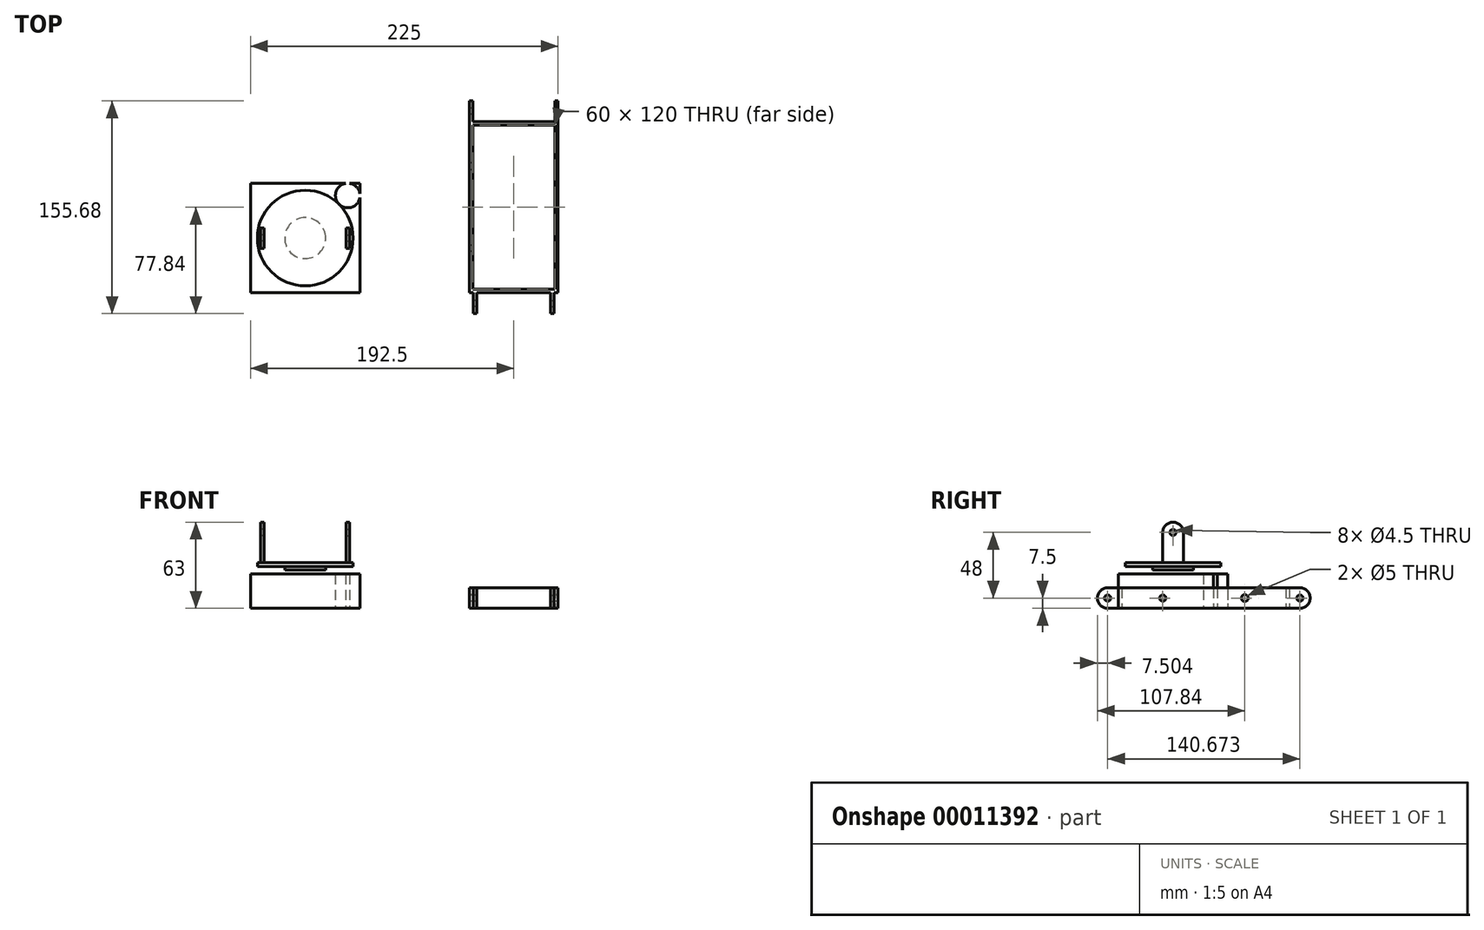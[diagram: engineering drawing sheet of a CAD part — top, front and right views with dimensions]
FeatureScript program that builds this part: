
annotation { "Feature Type Name" : "Feature", "Feature Type Description" : "" }
export const myFeature = defineFeature(function(context is Context, id is Id, definition is map)
    precondition{}
    {
        {
            var Q0;
            Q0=qCreatedBy(makeId("Top.planeOp"),FACE);
            var sketch = newSketch(context, id + "F0", { "sketchPlane" : qUnion([Q0])});
            skLineSegment(sketch, "E0.bottom", {"start": v(0, 120) * mm, "end": v(60, 120) * mm});
            skLineSegment(sketch, "E0.top", {"start": v(0, 0) * mm, "end": v(60, 0) * mm});
            skLineSegment(sketch, "E0.left", {"start": v(0, 120) * mm, "end": v(0, 0) * mm});
            skLineSegment(sketch, "E0.right", {"start": v(60, 120) * mm, "end": v(60, 0) * mm});
            skLineSegment(sketch, "E1", {"start": v(0, 90) * mm, "end": v(60, 90) * mm, "construction": true});
            skLineSegment(sketch, "E2", {"start": v(0, 30) * mm, "end": v(60, 30) * mm, "construction": true});
            skLineSegment(sketch, "E3.0", {"start": v(-2.5, 122.5) * mm, "end": v(62.5, 122.5) * mm});
            skLineSegment(sketch, "E3.1", {"start": v(-2.5, 122.5) * mm, "end": v(-2.5, -2.5) * mm});
            skLineSegment(sketch, "E3.2", {"start": v(-2.5, -2.5) * mm, "end": v(62.5, -2.5) * mm});
            skLineSegment(sketch, "E3.3", {"start": v(62.5, 122.5) * mm, "end": v(62.5, -2.5) * mm});
            skSolve(sketch);
        }
        {
            var Q0;
            Q0=makeQuery(id+"F0.imprint","IMPRINT",FACE,{"disambiguationData":[TD([[makeQuery(id+"F0.imprint","IMPRINT",EDGE,{"derivedFrom":sQuery(id+"F0.wireOp",EDGE,"E0.bottom")}),1.0]])]});
            extrude(context, id + "F1", {"entities" : qUnion([Q0]), "depth" : 15 * mm});
        }
        {
            var Q0;
            Q0=makeQuery(id+"F1.opExtrude","SWEPT_FACE",FACE,{"disambiguationData":[OSD([sQuery(id+"F0.wireOp",EDGE,"E3.1")])]});
            var sketch = newSketch(context, id + "F2", { "sketchPlane" : qUnion([Q0])});
            skLineSegment(sketch, "E4", {"start": v(-30, 0) * mm, "end": v(-30, 15) * mm, "construction": true});
            skCircle(sketch, "E5", {"center": v(-30, 7.5) * mm, "radius": 2.25 * mm});
            skLineSegment(sketch, "E6", {"start": v(-90, 0) * mm, "end": v(-90, 15) * mm, "construction": true});
            skCircle(sketch, "E7", {"center": v(-90, 7.5) * mm, "radius": 2.25 * mm});
            skLineSegment(sketch, "E8.bottom", {"start": v(-122.5, 0) * mm, "end": v(-130.34, 0) * mm});
            skLineSegment(sketch, "E8.top", {"start": v(-122.5, 15) * mm, "end": v(-130.34, 15) * mm});
            skLineSegment(sketch, "E8.left", {"start": v(-122.5, 0) * mm, "end": v(-122.5, 15) * mm});
            skLineSegment(sketch, "E8.right", {"start": v(-130.34, 0) * mm, "end": v(-130.34, 15) * mm});
            skArc(sketch, "E9", {"start": v(-130.34, 15) * mm, "mid": v(-137.84, 7.5) * mm, "end": v(-130.34, 0) * mm});
            skLineSegment(sketch, "E10", {"start": v(-130.34, 7.5) * mm, "end": v(-137.84, 7.5) * mm, "construction": true});
            skCircle(sketch, "E11", {"center": v(-130.34, 7.5) * mm, "radius": 2.25 * mm});
            skSolve(sketch);
        }
        {
            var Q0;
            Q0=sQuery(id+"F2.wireOp",VERTEX,"E5.center");
            var Q1;
            Q1=makeQuery(id+"F1.opExtrude","SWEPT_BODY",BODY,{"disambiguationData":[OSD([sQuery(id+"F0.wireOp",EDGE,"E0.bottom"),sQuery(id+"F0.wireOp",EDGE,"E0.top"),sQuery(id+"F0.wireOp",EDGE,"E0.left"),sQuery(id+"F0.wireOp",EDGE,"E0.right"),sQuery(id+"F0.wireOp",EDGE,"E3.0"),sQuery(id+"F0.wireOp",EDGE,"E3.1"),sQuery(id+"F0.wireOp",EDGE,"E3.2"),sQuery(id+"F0.wireOp",EDGE,"E3.3")])]});
            hole(context, id + "F3", {"style" : HoleStyle.SIMPLE, "holeDiameter" : 4.5 * mm, "endStyle" : HoleEndStyle.THROUGH, "locations" : qUnion([Q0]), "scope" : qUnion([Q1])});
        }
        {
            var Q0;
            Q0=sQuery(id+"F2.wireOp",VERTEX,"E7.center");
            var Q1;
            Q1=makeQuery(id+"F1.opExtrude","SWEPT_BODY",BODY,{"disambiguationData":[OSD([sQuery(id+"F0.wireOp",EDGE,"E0.bottom"),sQuery(id+"F0.wireOp",EDGE,"E0.top"),sQuery(id+"F0.wireOp",EDGE,"E0.left"),sQuery(id+"F0.wireOp",EDGE,"E0.right"),sQuery(id+"F0.wireOp",EDGE,"E3.0"),sQuery(id+"F0.wireOp",EDGE,"E3.1"),sQuery(id+"F0.wireOp",EDGE,"E3.2"),sQuery(id+"F0.wireOp",EDGE,"E3.3")])]});
            hole(context, id + "F4", {"style" : HoleStyle.SIMPLE, "holeDiameter" : 5 * mm, "endStyle" : HoleEndStyle.THROUGH, "locations" : qUnion([Q0]), "scope" : qUnion([Q1])});
        }
        {
            var Q0;
            Q0=makeQuery(id+"F1.opExtrude","SWEPT_FACE",FACE,{"disambiguationData":[OSD([sQuery(id+"F0.wireOp",EDGE,"E0.left")])]});
            cPlane(context, id + "F5", {"entities" : qUnion([Q0]), "cplaneType" : CPlaneType.OFFSET, "offset" : .5 * mm, "width" : 150 * mm, "height" : 150 * mm});
        }
        {
            var Q0;
            Q0=qCreatedBy(id+"F5.planeOp",FACE);
            var sketch = newSketch(context, id + "F6", { "sketchPlane" : qUnion([Q0])});
            skLineSegment(sketch, "E12.bottom", {"start": v(-2.5, 15) * mm, "end": v(-10.34, 15) * mm});
            skLineSegment(sketch, "E12.top", {"start": v(-2.5, 0) * mm, "end": v(-10.34, 0) * mm});
            skLineSegment(sketch, "E12.left", {"start": v(-2.5, 15) * mm, "end": v(-2.5, 0) * mm});
            skLineSegment(sketch, "E12.right", {"start": v(-10.34, 15) * mm, "end": v(-10.34, 0) * mm});
            skArc(sketch, "E13", {"start": v(-10.34, 15) * mm, "mid": v(-17.84, 7.5) * mm, "end": v(-10.34, 0) * mm});
            skCircle(sketch, "E14", {"center": v(-10.34, 7.5) * mm, "radius": 2.25 * mm});
            skSolve(sketch);
        }
        {
            var Q0;
            Q0=makeQuery(id+"F1.opExtrude","SWEPT_FACE",FACE,{"disambiguationData":[OSD([sQuery(id+"F0.wireOp",EDGE,"E3.3")])]});
            var sketch = newSketch(context, id + "F7", { "sketchPlane" : qUnion([Q0])});
            skLineSegment(sketch, "E15.bottom", {"start": v(122.5, 15) * mm, "end": v(130.34, 15) * mm});
            skLineSegment(sketch, "E15.top", {"start": v(122.5, 0) * mm, "end": v(130.34, 0) * mm});
            skLineSegment(sketch, "E15.left", {"start": v(122.5, 15) * mm, "end": v(122.5, 0) * mm});
            skLineSegment(sketch, "E15.right", {"start": v(130.34, 15) * mm, "end": v(130.34, 0) * mm});
            skArc(sketch, "E16", {"start": v(130.34, 0) * mm, "mid": v(137.84, 7.5) * mm, "end": v(130.34, 15) * mm});
            skCircle(sketch, "E17", {"center": v(130.34, 7.5) * mm, "radius": 2.25 * mm});
            skSolve(sketch);
        }
        {
            var Q0;
            Q0=makeQuery(id+"F1.opExtrude","SWEPT_FACE",FACE,{"disambiguationData":[OSD([sQuery(id+"F0.wireOp",EDGE,"E0.right")])]});
            cPlane(context, id + "F8", {"entities" : qUnion([Q0]), "cplaneType" : CPlaneType.OFFSET, "offset" : 0.5 * mm, "width" : 150 * mm, "height" : 150 * mm});
        }
        {
            var Q0;
            Q0=qCreatedBy(id+"F8.planeOp",FACE);
            var sketch = newSketch(context, id + "F9", { "sketchPlane" : qUnion([Q0])});
            skLineSegment(sketch, "E18.bottom", {"start": v(2.5, 0) * mm, "end": v(10.34, 0) * mm});
            skLineSegment(sketch, "E18.top", {"start": v(2.5, 15) * mm, "end": v(10.34, 15) * mm});
            skLineSegment(sketch, "E18.left", {"start": v(2.5, 0) * mm, "end": v(2.5, 15) * mm});
            skLineSegment(sketch, "E18.right", {"start": v(10.34, 0) * mm, "end": v(10.34, 15) * mm});
            skArc(sketch, "E19", {"start": v(10.34, 0) * mm, "mid": v(17.84, 7.5) * mm, "end": v(10.34, 15) * mm});
            skCircle(sketch, "E20", {"center": v(10.34, 7.5) * mm, "radius": 2.25 * mm});
            skSolve(sketch);
        }
        {
            var Q0;
            {var subQ6=sQuery(id+"F9.wireOp",EDGE,"E18.bottom");Q0=makeQuery(id+"F9.imprint","IMPRINT",FACE,{"disambiguationData":[TD([[makeQuery(id+"F9.imprint","IMPRINT",EDGE,{"derivedFrom":subQ6}),1.0]])]});}
            var Q1;
            {var subQ4=sQuery(id+"F9.wireOp",EDGE,"E19");Q1=makeQuery(id+"F9.imprint","IMPRINT",FACE,{"disambiguationData":[TD([[makeQuery(id+"F9.imprint","IMPRINT",EDGE,{"derivedFrom":subQ4}),1.0]])]});}
            extrude(context, id + "F10", {"entities" : qUnion([Q0, Q1]), "operationType" : NewBodyOperationType.ADD, "depth" : 2.5 * mm});
        }
        {
            var Q0;
            {var subQ6=sQuery(id+"F6.wireOp",EDGE,"E12.bottom");Q0=makeQuery(id+"F6.imprint","IMPRINT",FACE,{"disambiguationData":[TD([[makeQuery(id+"F6.imprint","IMPRINT",EDGE,{"derivedFrom":subQ6}),1.0]])]});}
            var Q1;
            {var subQ4=sQuery(id+"F6.wireOp",EDGE,"E13");Q1=makeQuery(id+"F6.imprint","IMPRINT",FACE,{"disambiguationData":[TD([[makeQuery(id+"F6.imprint","IMPRINT",EDGE,{"derivedFrom":subQ4}),1.0]])]});}
            extrude(context, id + "F11", {"entities" : qUnion([Q0, Q1]), "operationType" : NewBodyOperationType.ADD, "depth" : 2.5 * mm});
        }
        {
            var Q0;
            {var subQ6=sQuery(id+"F7.wireOp",EDGE,"E15.bottom");Q0=makeQuery(id+"F7.imprint","IMPRINT",FACE,{"disambiguationData":[TD([[makeQuery(id+"F7.imprint","IMPRINT",EDGE,{"derivedFrom":subQ6}),-1.0]])]});}
            var Q1;
            {var subQ4=sQuery(id+"F7.wireOp",EDGE,"E16");Q1=makeQuery(id+"F7.imprint","IMPRINT",FACE,{"disambiguationData":[TD([[makeQuery(id+"F7.imprint","IMPRINT",EDGE,{"derivedFrom":subQ4}),1.0]])]});}
            extrude(context, id + "F12", {"entities" : qUnion([Q0, Q1]), "operationType" : NewBodyOperationType.ADD, "oppositeDirection" : true, "depth" : 2.5 * mm});
        }
        {
            var Q0;
            {var subQ6=sQuery(id+"F2.wireOp",EDGE,"E8.bottom");Q0=makeQuery(id+"F2.imprint","IMPRINT",FACE,{"disambiguationData":[TD([[makeQuery(id+"F2.imprint","IMPRINT",EDGE,{"derivedFrom":subQ6}),-1.0]])]});}
            var Q1;
            {var subQ4=sQuery(id+"F2.wireOp",EDGE,"E9");Q1=makeQuery(id+"F2.imprint","IMPRINT",FACE,{"disambiguationData":[TD([[makeQuery(id+"F2.imprint","IMPRINT",EDGE,{"derivedFrom":subQ4}),1.0]])]});}
            extrude(context, id + "F13", {"entities" : qUnion([Q0, Q1]), "operationType" : NewBodyOperationType.ADD, "oppositeDirection" : true, "depth" : 2.5 * mm});
        }
        {
            var Q0;
            Q0=qCreatedBy(makeId("Top.planeOp"),FACE);
            var sketch = newSketch(context, id + "F14", { "sketchPlane" : qUnion([Q0])});
            skLineSegment(sketch, "E21.bottom", {"start": v(-162.5, -2.5) * mm, "end": v(-82.5, -2.5) * mm});
            skLineSegment(sketch, "E21.top", {"start": v(-162.5, 77.5) * mm, "end": v(-82.5, 77.5) * mm});
            skLineSegment(sketch, "E21.left", {"start": v(-162.5, -2.5) * mm, "end": v(-162.5, 77.5) * mm});
            skLineSegment(sketch, "E21.right", {"start": v(-82.5, -2.5) * mm, "end": v(-82.5, 77.5) * mm});
            skCircle(sketch, "E22", {"center": v(-122.5, 37.5) * mm, "radius": 35 * mm});
            skLineSegment(sketch, "E23", {"start": v(-122.5, 77.5) * mm, "end": v(-122.5, -2.5) * mm, "construction": true});
            skLineSegment(sketch, "E24", {"start": v(-82.5, 37.5) * mm, "end": v(-162.5, 37.5) * mm, "construction": true});
            skLineSegment(sketch, "E25", {"start": v(-90, 45) * mm, "end": v(-90, 30) * mm, "construction": true});
            skLineSegment(sketch, "E26.MirrorCS", {"start": v(-155, 45) * mm, "end": v(-155, 30) * mm, "construction": true});
            skCircle(sketch, "E27", {"center": v(-122.5, 37.5) * mm, "radius": 15 * mm});
            skLineSegment(sketch, "E28", {"start": v(-147.25, 12.75) * mm, "end": v(-122.5, 37.5) * mm, "construction": true});
            skLineSegment(sketch, "E29", {"start": v(-82.5, 77.5) * mm, "end": v(-147.25, 12.75) * mm, "construction": true});
            skCircle(sketch, "E30", {"center": v(-91.39, 68.61) * mm, "radius": 9 * mm});
            skLineSegment(sketch, "E31.bottom", {"start": v(-90, 45) * mm, "end": v(-92.5, 45) * mm});
            skLineSegment(sketch, "E31.top", {"start": v(-90, 30) * mm, "end": v(-92.5, 30) * mm});
            skLineSegment(sketch, "E31.left", {"start": v(-90, 45) * mm, "end": v(-90, 30) * mm});
            skLineSegment(sketch, "E31.right", {"start": v(-92.5, 45) * mm, "end": v(-92.5, 30) * mm});
            skLineSegment(sketch, "E32.MirrorCS", {"start": v(-152.5, 45) * mm, "end": v(-152.5, 30) * mm});
            skLineSegment(sketch, "E33.MirrorCS", {"start": v(-155, 45) * mm, "end": v(-152.5, 45) * mm});
            skLineSegment(sketch, "E34.MirrorCS", {"start": v(-155, 45) * mm, "end": v(-155, 30) * mm});
            skLineSegment(sketch, "E35.MirrorCS", {"start": v(-155, 30) * mm, "end": v(-152.5, 30) * mm});
            skPoint(sketch, "E36", {"position": v(-90, 37.5) * mm});
            skSolve(sketch);
        }
        {
            var Q0;
            {var subQ5=sQuery(id+"F14.wireOp",EDGE,"E21.bottom");Q0=makeQuery(id+"F14.imprint","IMPRINT",FACE,{"disambiguationData":[TD([[makeQuery(id+"F14.imprint","IMPRINT",EDGE,{"derivedFrom":subQ5}),1.0]])]});}
            var Q1;
            Q1=makeQuery(id+"F14.imprint","IMPRINT",FACE,{"disambiguationData":[TD([[makeQuery(id+"F14.imprint","IMPRINT",EDGE,{"derivedFrom":sQuery(id+"F14.wireOp",EDGE,"E22")}),1.0]])]});
            var Q2;
            {var subQ0=sQuery(id+"F14.wireOp",EDGE,"E30");var subQ4=sQuery(id+"F14.wireOp",EDGE,"E21.top");var subQ5=makeQuery(id+"F14.imprint","INTERSECT",VERTEX,{"disambiguationData":[OD(0.0)],"derivedFrom":[subQ4,subQ0]});Q2=makeQuery(id+"F14.imprint","IMPRINT",FACE,{"disambiguationData":[TD([[makeQuery(id+"F14.imprint","IMPRINT",EDGE,{"disambiguationData":[TD([[subQ5,-1.0]])],"derivedFrom":subQ4}),-1.0]])]});}
            var Q3;
            {var subQ1=sQuery(id+"F14.wireOp",EDGE,"E21.right");var subQ3=sQuery(id+"F14.wireOp",EDGE,"E21.top");var subQ5=makeQuery(id+"F14.imprint","INTERSECT",VERTEX,{"derivedFrom":[subQ3,subQ1]});Q3=makeQuery(id+"F14.imprint","IMPRINT",FACE,{"disambiguationData":[TD([[makeQuery(id+"F14.imprint","IMPRINT",EDGE,{"disambiguationData":[TD([[subQ5,1.0]])],"derivedFrom":subQ3}),-1.0]])]});}
            var Q4;
            Q4=makeQuery(id+"F14.imprint","IMPRINT",FACE,{"disambiguationData":[TD([[makeQuery(id+"F14.imprint","IMPRINT",EDGE,{"derivedFrom":sQuery(id+"F14.wireOp",EDGE,"E31.bottom")}),1.0]])]});
            var Q5;
            Q5=makeQuery(id+"F14.imprint","IMPRINT",FACE,{"disambiguationData":[TD([[makeQuery(id+"F14.imprint","IMPRINT",EDGE,{"derivedFrom":sQuery(id+"F14.wireOp",EDGE,"E32.MirrorCS")}),-1.0]])]});
            var Q6;
            Q6=makeQuery(id+"F14.imprint","IMPRINT",FACE,{"disambiguationData":[TD([[makeQuery(id+"F14.imprint","IMPRINT",EDGE,{"derivedFrom":sQuery(id+"F14.wireOp",EDGE,"E27")}),1.0]])]});
            extrude(context, id + "F15", {"entities" : qUnion([Q0, Q1, Q2, Q3, Q4, Q5, Q6]), "depth" : 25 * mm});
        }
        {
            var Q0;
            Q0=makeQuery(id+"F15.opExtrude","CAP_FACE",FACE,{"disambiguationData":[OSD([sQuery(id+"F14.wireOp",EDGE,"E21.bottom"),sQuery(id+"F14.wireOp",EDGE,"E21.top"),sQuery(id+"F14.wireOp",EDGE,"E21.left"),sQuery(id+"F14.wireOp",EDGE,"E21.right")])],"isStart":false});
            cPlane(context, id + "F16", {"entities" : qUnion([Q0]), "cplaneType" : CPlaneType.OFFSET, "offset" : 3 * mm, "width" : 150 * mm, "height" : 150 * mm});
        }
        {
            var Q0;
            Q0=qCreatedBy(id+"F16.planeOp",FACE);
            var sketch = newSketch(context, id + "F17", { "sketchPlane" : qUnion([Q0])});
            skCircle(sketch, "E37.0", {"center": v(-122.5, 37.5) * mm, "radius": 15 * mm});
            skSolve(sketch);
        }
        {
            var Q0;
            Q0=makeQuery(id+"F17.imprint","IMPRINT",FACE,{"disambiguationData":[TD([[makeQuery(id+"F17.imprint","IMPRINT",EDGE,{"derivedFrom":sQuery(id+"F17.wireOp",EDGE,"E37.0")}),1.0]])]});
            extrude(context, id + "F18", {"entities" : qUnion([Q0]), "depth" : 2.5 * mm});
        }
        {
            var Q0;
            Q0=makeQuery(id+"F18.opExtrude","CAP_FACE",FACE,{"disambiguationData":[OSD([sQuery(id+"F17.wireOp",EDGE,"E37.0")])],"isStart":false});
            var sketch = newSketch(context, id + "F19", { "sketchPlane" : qUnion([Q0])});
            skCircle(sketch, "E38.0", {"center": v(-122.5, 37.5) * mm, "radius": 35 * mm});
            skLineSegment(sketch, "E39.0", {"start": v(-155, 45) * mm, "end": v(-155, 30) * mm});
            skLineSegment(sketch, "E39.1", {"start": v(-155, 30) * mm, "end": v(-152.5, 30) * mm});
            skLineSegment(sketch, "E39.2", {"start": v(-152.5, 45) * mm, "end": v(-152.5, 30) * mm});
            skLineSegment(sketch, "E39.3", {"start": v(-155, 45) * mm, "end": v(-152.5, 45) * mm});
            skLineSegment(sketch, "E39.4", {"start": v(-92.5, 45) * mm, "end": v(-92.5, 30) * mm});
            skLineSegment(sketch, "E39.5", {"start": v(-90, 45) * mm, "end": v(-92.5, 45) * mm});
            skLineSegment(sketch, "E39.6", {"start": v(-90, 45) * mm, "end": v(-90, 30) * mm});
            skLineSegment(sketch, "E39.7", {"start": v(-90, 30) * mm, "end": v(-92.5, 30) * mm});
            skSolve(sketch);
        }
        {
            var Q0;
            Q0=makeQuery(id+"F19.imprint","IMPRINT",FACE,{"disambiguationData":[TD([[makeQuery(id+"F19.imprint","IMPRINT",EDGE,{"derivedFrom":sQuery(id+"F19.wireOp",EDGE,"E39.4")}),1.0]])]});
            var Q1;
            Q1=makeQuery(id+"F19.imprint","IMPRINT",FACE,{"disambiguationData":[TD([[makeQuery(id+"F19.imprint","IMPRINT",EDGE,{"derivedFrom":sQuery(id+"F19.wireOp",EDGE,"E39.0")}),1.0]])]});
            extrude(context, id + "F20", {"entities" : qUnion([Q0, Q1]), "operationType" : NewBodyOperationType.ADD, "depth" : 25 * mm});
        }
        {
            var Q0;
            Q0=makeQuery(id+"F19.imprint","IMPRINT",FACE,{"disambiguationData":[TD([[makeQuery(id+"F19.imprint","IMPRINT",EDGE,{"derivedFrom":sQuery(id+"F19.wireOp",EDGE,"E38.0")}),1.0]])]});
            var Q1;
            Q1=makeQuery(id+"F19.imprint","IMPRINT",FACE,{"disambiguationData":[TD([[makeQuery(id+"F19.imprint","IMPRINT",EDGE,{"derivedFrom":makeQuery(id+"F18.opExtrude","CAP_EDGE",EDGE,{"disambiguationData":[OSD([sQuery(id+"F17.wireOp",EDGE,"E37.0")])],"isStart":false})}),1.0]])]});
            extrude(context, id + "F21", {"entities" : qUnion([Q0, Q1]), "operationType" : NewBodyOperationType.ADD, "depth" : 3 * mm});
        }
        {
            var Q0;
            Q0=makeQuery(id+"F20.opExtrude","SWEPT_FACE",FACE,{"disambiguationData":[OSD([sQuery(id+"F19.wireOp",EDGE,"E39.6")])]});
            var sketch = newSketch(context, id + "F22", { "sketchPlane" : qUnion([Q0])});
            skArc(sketch, "E40", {"start": v(45, 55.5) * mm, "mid": v(37.5, 63) * mm, "end": v(30, 55.5) * mm});
            skCircle(sketch, "E41", {"center": v(37.5, 55.5) * mm, "radius": 2.25 * mm});
            skSolve(sketch);
        }
        {
            var Q0;
            Q0=makeQuery(id+"F20.opExtrude","SWEPT_FACE",FACE,{"disambiguationData":[OSD([sQuery(id+"F19.wireOp",EDGE,"E39.0")])]});
            var sketch = newSketch(context, id + "F23", { "sketchPlane" : qUnion([Q0])});
            skArc(sketch, "E42", {"start": v(-30, 55.5) * mm, "mid": v(-37.5, 63) * mm, "end": v(-45, 55.5) * mm});
            skCircle(sketch, "E43", {"center": v(-37.5, 55.5) * mm, "radius": 2.25 * mm});
            skSolve(sketch);
        }
        {
            var Q0;
            {var subQ4=sQuery(id+"F22.wireOp",EDGE,"E40");Q0=makeQuery(id+"F22.imprint","IMPRINT",FACE,{"disambiguationData":[TD([[makeQuery(id+"F22.imprint","IMPRINT",EDGE,{"derivedFrom":subQ4}),1.0]])]});}
            extrude(context, id + "F24", {"entities" : qUnion([Q0]), "operationType" : NewBodyOperationType.ADD, "oppositeDirection" : true, "depth" : 2.5 * mm});
        }
        {
            var Q0;
            {var subQ0=makeQuery(id+"F20.opExtrude","CAP_EDGE",EDGE,{"disambiguationData":[OSD([sQuery(id+"F19.wireOp",EDGE,"E39.6")])],"isStart":false});var subQ1=sQuery(id+"F22.wireOp",EDGE,"E41");var subQ3=makeQuery(id+"F22.imprint","INTERSECT",VERTEX,{"disambiguationData":[OD(0.0)],"derivedFrom":[subQ0,subQ1]});Q0=makeQuery(id+"F22.imprint","IMPRINT",FACE,{"disambiguationData":[TD([[makeQuery(id+"F22.imprint","IMPRINT",EDGE,{"disambiguationData":[TD([[subQ3,1.0]])],"derivedFrom":subQ1}),1.0]])]});}
            extrude(context, id + "F25", {"entities" : qUnion([Q0]), "operationType" : NewBodyOperationType.REMOVE, "oppositeDirection" : true, "depth" : 25 * mm});
        }
        {
            var Q0;
            {var subQ4=sQuery(id+"F23.wireOp",EDGE,"E42");Q0=makeQuery(id+"F23.imprint","IMPRINT",FACE,{"disambiguationData":[TD([[makeQuery(id+"F23.imprint","IMPRINT",EDGE,{"derivedFrom":subQ4}),1.0]])]});}
            extrude(context, id + "F26", {"entities" : qUnion([Q0]), "operationType" : NewBodyOperationType.ADD, "oppositeDirection" : true, "depth" : 2.5 * mm});
        }
        {
            var Q0;
            {var subQ0=makeQuery(id+"F20.opExtrude","CAP_EDGE",EDGE,{"disambiguationData":[OSD([sQuery(id+"F19.wireOp",EDGE,"E39.0")])],"isStart":false});var subQ1=sQuery(id+"F23.wireOp",EDGE,"E43");var subQ3=makeQuery(id+"F23.imprint","INTERSECT",VERTEX,{"disambiguationData":[OD(0.0)],"derivedFrom":[subQ0,subQ1]});Q0=makeQuery(id+"F23.imprint","IMPRINT",FACE,{"disambiguationData":[TD([[makeQuery(id+"F23.imprint","IMPRINT",EDGE,{"disambiguationData":[TD([[subQ3,-1.0]])],"derivedFrom":subQ1}),1.0]])]});}
            extrude(context, id + "F27", {"entities" : qUnion([Q0]), "operationType" : NewBodyOperationType.REMOVE, "oppositeDirection" : true, "depth" : 2.5 * mm});
        }
    });
